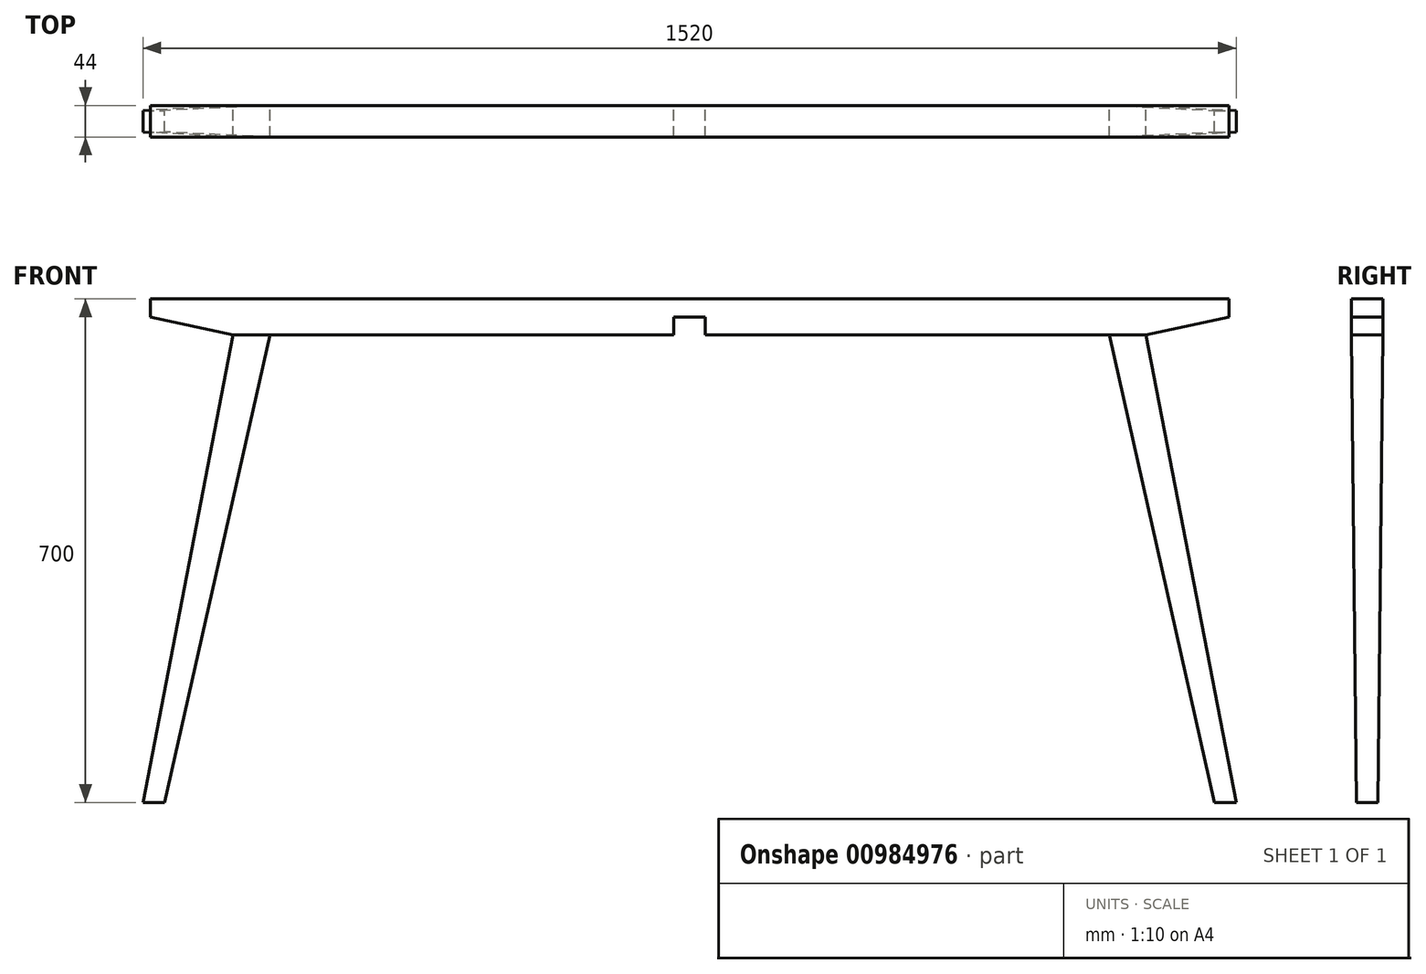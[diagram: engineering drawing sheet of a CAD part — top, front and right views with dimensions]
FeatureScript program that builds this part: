
annotation { "Feature Type Name" : "Feature", "Feature Type Description" : "" }
export const myFeature = defineFeature(function(context is Context, id is Id, definition is map)
    precondition{}
    {
        {
            var Q0;
            Q0=qCreatedBy(makeId("Front.planeOp"),FACE);
            var sketch = newSketch(context, id + "F0", { "sketchPlane" : qUnion([Q0])});
            skLineSegment(sketch, "E0", {"start": v(0, -50) * mm, "end": v(0, -700) * mm, "construction": true});
            skLineSegment(sketch, "E1", {"start": v(0, -700) * mm, "end": v(-80.07, -700) * mm, "construction": true});
            skLineSegment(sketch, "E2", {"start": v(-22, 0) * mm, "end": v(-750, 0) * mm});
            skLineSegment(sketch, "E3", {"start": v(-750, 0) * mm, "end": v(-625, 0) * mm, "construction": true});
            skLineSegment(sketch, "E4", {"start": v(-750, 0) * mm, "end": v(-750, -25) * mm});
            skLineSegment(sketch, "E5", {"start": v(-760, -700) * mm, "end": v(-634.64, -50) * mm});
            skLineSegment(sketch, "E6.0", {"start": v(-22, -50) * mm, "end": v(-583.72, -50) * mm});
            skLineSegment(sketch, "E7", {"start": v(-750, 0) * mm, "end": v(-750, -25) * mm, "construction": true});
            skLineSegment(sketch, "E8", {"start": v(-750, -25) * mm, "end": v(-634.64, -50) * mm});
            skLineSegment(sketch, "E9", {"start": v(-760, -700) * mm, "end": v(-730, -700) * mm});
            skLineSegment(sketch, "E10", {"start": v(-730, -700) * mm, "end": v(-583.72, -50) * mm});
            skLineSegment(sketch, "E11.MirrorCS", {"start": v(22, 0) * mm, "end": v(750, 0) * mm});
            skLineSegment(sketch, "E12.MirrorCS", {"start": v(750, 0) * mm, "end": v(750, -25) * mm});
            skLineSegment(sketch, "E13.MirrorCS", {"start": v(750, -25) * mm, "end": v(634.64, -50) * mm});
            skLineSegment(sketch, "E14.MirrorCS", {"start": v(760, -700) * mm, "end": v(634.64, -50) * mm});
            skLineSegment(sketch, "E15.MirrorCS", {"start": v(730, -700) * mm, "end": v(583.72, -50) * mm});
            skLineSegment(sketch, "E16.MirrorCS", {"start": v(22, -50) * mm, "end": v(583.72, -50) * mm});
            skLineSegment(sketch, "E17.MirrorCS", {"start": v(760, -700) * mm, "end": v(730, -700) * mm});
            skLineSegment(sketch, "E18", {"start": v(-22, -25) * mm, "end": v(0, -25) * mm});
            skLineSegment(sketch, "E19.MirrorCS", {"start": v(22, -25) * mm, "end": v(0, -25) * mm});
            skPoint(sketch, "E20.orphan", {"position": v(0, 0) * mm});
            skLineSegment(sketch, "E21", {"start": v(-22, 0) * mm, "end": v(22, 0) * mm});
            skLineSegment(sketch, "E22.MirrorCS", {"start": v(-22, -50) * mm, "end": v(-22, -25) * mm});
            skLineSegment(sketch, "E23.MirrorCS", {"start": v(22, -50) * mm, "end": v(22, -25) * mm});
            skPoint(sketch, "E24.MirrorCS.end.orphan", {"position": v(22, -25) * mm});
            skPoint(sketch, "E25.orphan", {"position": v(0, -50) * mm});
            skSolve(sketch);
        }
        {
            var Q0;
            Q0=qSketchRegion(id+"F0",true);
            extrude(context, id + "F1", {"entities" : qUnion([Q0]), "depth" : 44 * mm, "offsetDistance" : 25 * mm});
        }
        {
            var Q0;
            Q0=qCreatedBy(makeId("Right.planeOp"),FACE);
            var sketch = newSketch(context, id + "F2", { "sketchPlane" : qUnion([Q0])});
            skLineSegment(sketch, "E26", {"start": v(0, 0) * mm, "end": v(0, -50) * mm, "construction": true});
            skLineSegment(sketch, "E27", {"start": v(0, -50) * mm, "end": v(0, -700) * mm});
            skLineSegment(sketch, "E28", {"start": v(-22, -700) * mm, "end": v(-22, -631.39) * mm, "construction": true});
            skLineSegment(sketch, "E29", {"start": v(0, -700) * mm, "end": v(-7, -700) * mm});
            skLineSegment(sketch, "E30", {"start": v(-7, -700) * mm, "end": v(0, -50) * mm});
            skLineSegment(sketch, "E31.MirrorCS", {"start": v(-37, -700) * mm, "end": v(-44, -50) * mm});
            skLineSegment(sketch, "E32.MirrorCS", {"start": v(-44, -50) * mm, "end": v(-44, -700) * mm});
            skLineSegment(sketch, "E33.MirrorCS", {"start": v(-44, -700) * mm, "end": v(-37, -700) * mm});
            skSolve(sketch);
        }
        {
            var Q0;
            Q0=qSketchRegion(id+"F2",true);
            extrude(context, id + "F3", {"entities" : qUnion([Q0]), "operationType" : NewBodyOperationType.REMOVE, "endBound" : BoundingType.SYMMETRIC, "oppositeDirection" : true, "depth" : 1808 * mm, "offsetDistance" : 25 * mm});
        }
    });
